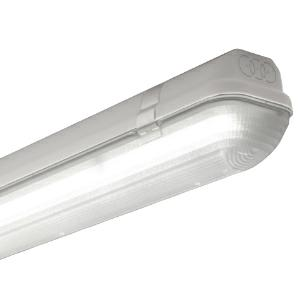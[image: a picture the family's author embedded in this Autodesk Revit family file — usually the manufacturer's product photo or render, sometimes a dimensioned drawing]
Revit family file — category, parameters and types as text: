
# Revit family: 3f_filippi_-_3f_linda_3f_filippi_-_58613_-_3f_linda_led_1x30w-830_ep_l1570
name_source: partatom
category: Lighting Fixtures
units: mm (PartAtom-declared; Revit-internal decimal feet)

## family parameters
Cut with Voids When Loaded = No
Host = Face
Light Source = No
Part Type = Normal
Room Calculation Point = No
Round Connector Dimension = Use Diameter
Shared = No

## types (1)
- 3F Filippi - 3F Linda (1 x LED, 4921 lm, 34.5 W, 3000 K)
    Apparent Load = 35 VA
    Approval mark = ENEC
    CIE Flux Codes = 44 77 94 97 100
    Color Rendering = 80
    Color Temperature = 3000 K
    Control Gear = Electronic ballast
    Default Elevation = 1800 mm
    Description = ILLUMINOTECHNICAL
Luminous efficiency 100% (DLOR 97%, ULOR 3%).
Initial luminous flux of the luminaire 4921 lm.
Emergency luminaire luminous flux BLF 11.4%.
Controlled symmetric distribution.
Installation Interdistance Transv.D = 1.77 x hu - Long.D = 1.17 x hu.
Tabular UGR (CIE 117 - 4H-8H; S=0.25H; 70/50/20): RUG 21.9 - 22.9.
Beam angle: 109° - 64°.
Luminous efficacy 143 lm/W.
Lifetime (L93/B10): 30000 h. (tq+25°C)
Lifetime (L90/B10): 50000 h. (tq+25°C)
Lifetime (L85/B10): 80000 h. (tq+25°C)
Lifetime (L80/B10): 100000 h. (tq+25°C)
Sudden decreased luminous flux after 50000 hours: 0% (C0).
Photobiological safety in compliance with IEC/TR 62778: RG0 risk exempt, (IEC 62471).
In compliance with IEC/EN 62722-2-1 - IEC/EN 62717 standards.

SOURCE
Linear LED module 30W/830.
Energy efficiency class (UE 2019/2020 - UE 2019/2015): D.
CIE 13.3 Colour rendering index: CRI >80 (R9 <50%).
IES TM-30 Fidelity Index: Rf = 84 Rg = 95.
CCT nominal colour temperature 3000 K.
Colour initial tolerance (MacAdam): SDCM 3.

MECHANICAL
Self-extinguishing V2 polycarbonate housing, injection moulded, RAL 7035 grey.
Ecologic anti-aging injected sealing gasket.
Diffuser in self-extinguishing V2 polycarbonate, photo-engraved interior, UV stabilised, injection moulded with smooth outer surface, tamper-proof opening.
Gear-holder reflector in hot-dip galvanised steel, painted with white polyester base.
Snug fit safety snap-lock clips for diffuser mounting in stainless steel, screwdriver opening.
Fixing brackets in stainless steel.
Possibility for technicians to access the interior of the luminaire.
Luminaire with limited surface temperature. - D - (EN 60598-2-24)
Dimensions: 1570x100 mm, height 100 mm. Weight 2.89 kg.
IP66 protection degree.
Mechanical strength to impacts IK10 (20 joule).
Glow-wire test resistance 850°C.

ELECTRICAL
Halogen Free electronic wiring 230V-50/60Hz, power factor 0.90, THD <25%, constant output current, SELV, class I, 1 driver.
Power of the luminaire 34.5 W.
CE - IEC 60598-1 - EN 60598-1.
EP maintained emergency wiring on board, 1h duration, 24h recharge; compliant with EN 60598-2-22, excluding high risk areas.
SAFE FLICKER: PstLM=<1 and SVM=<0.4 (IEC TR 61547-1 and IEC TR 63158), to ensure a more comfortable and safe light.
Ambient temperature from +5°C to +25°C.
Temperature class T6 max 85°C.
Relative humidity UR: <85%.

INSTALLATION
Ceiling / Suspended / Wall.
All accessories dedicated to this product are available on the Catalog and on our website www.3F-Filippi.com.

APPLICATIONS
Suitable product for food production plants (HACCP), IFS (Food Version 6), BRC (GSFS Food Version 7).
Dry, dusty indoor environments, subject to occasional water splashes.
Virtually shatterproof polycarbonate compatibly with the fumes / atmospheres that compromise the elasticity of plastic materials.
Not suitable for installation on surfaces subject to important vibrations, exposed to weather conditions, on ropes or poles.
Suitable for illumination of public car parks and parking grounds referred to DIN 67528:2018-04.

WARNING
Fixture not suitable for cold stores with an ambient temperature <5°C and/or relative humidity >85%.
Luminaire designed for disposal/recycling at end-of-life.
Replaceable (LED only) light source by a professional. Replaceable control gear by a professional.
    Height = 100 mm  [stored 0.328084 ft]
    Lamp = 1 x LED
    Lamp Light Flux = 4921 lm
    Lamp Power = 34.5 W
    Lamp count = 1
    Length = 1570 mm
    Lifetime = 50000 h
    Luminous efficacy = 143 lm/W
    Manufacturer = 3F Filippi
    ModVariant = No
    Model = 3F Filippi - 58613 - 3F Linda LED 1x30W-830 EP L1570
    Mounting Place = Ceiling
    Mounting Type = Pendant
    Number of Poles = 1
    OnlyDefault = Yes
    Power Factor = 1
    Product Name = 3F Filippi - 3F Linda
    Product group = pendant luminaire
    ProductGroupID = 9
    Protection Class = Protection class I
    Protection Degree = IP 66
    RLX_Detail_Level = 1
    RLX_Emergency_Light_Flux = 0 lm
    RLX_Emergency_Type = 0
    RLX_Emergency_Type_DB = No
    RlxData = <blob elided: 70265 chars, md5=23e27b1a>
    Socket = socket
    Standby Power = 0 W
    System Light Flux = 4921 lm
    System Power = 35 W
    Type Comments = Product without accessories
    Type Image = 3ffilippi_3f_linda_led.jpg
    URL = http://relux.com
    VarID = ---
    Voltage = 0 V
    Weight = 0.00 kg
    Width = 100 mm  [stored 0.328084 ft]

note: [stored X ft] marks values corroborated as IEEE doubles in the binary element streams (Revit-internal decimal feet)

## geometry (parser evidence)
native form markers: Blend x4, Sweep x9
no freeform markers — native parametric forms only
